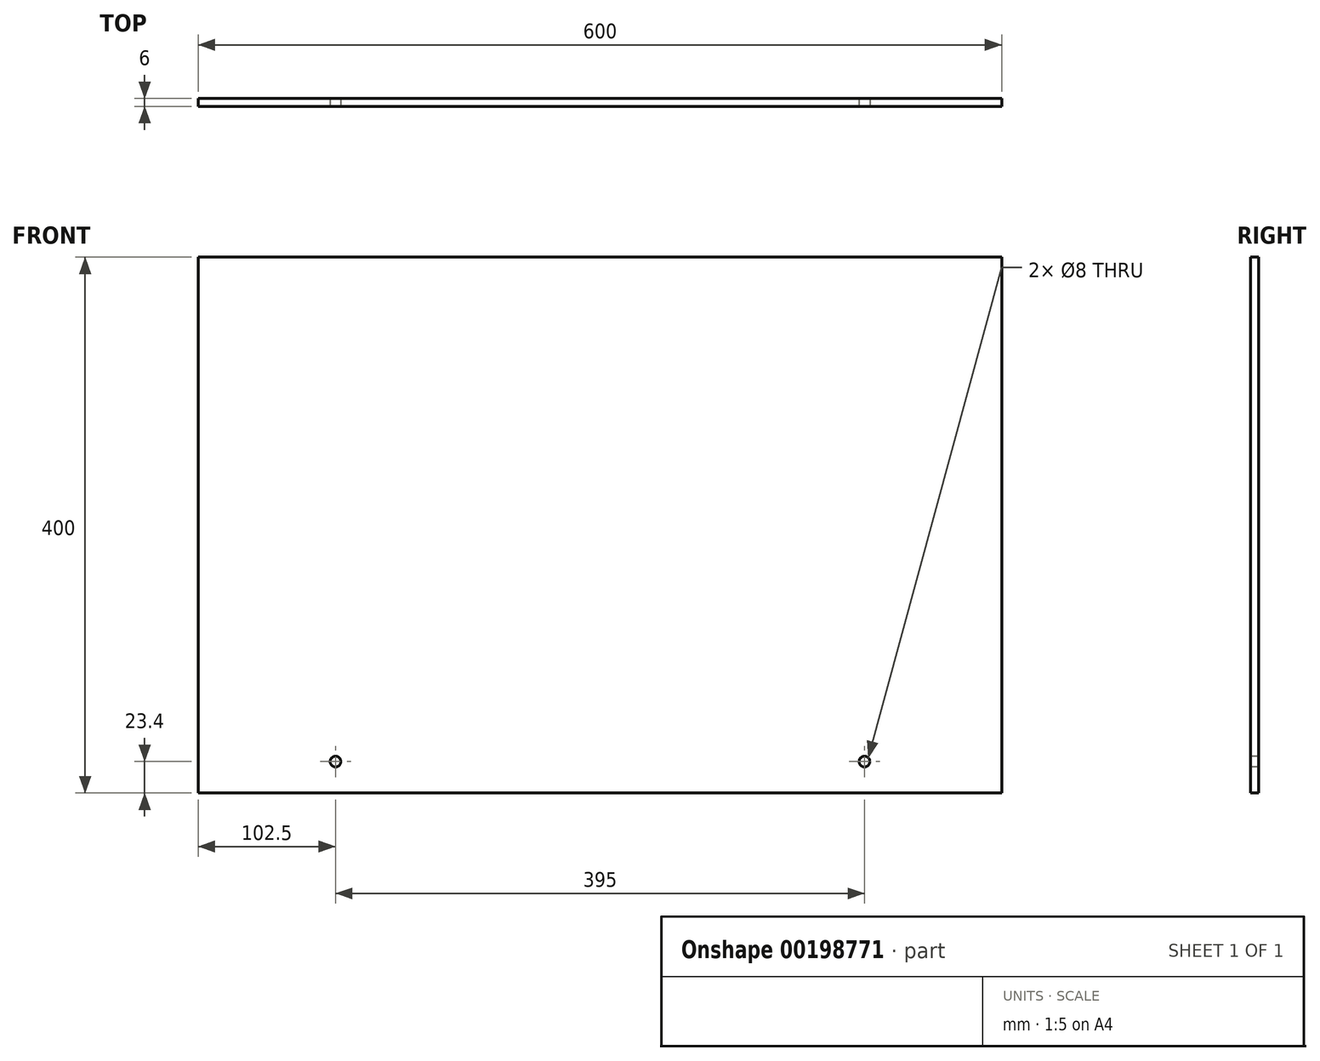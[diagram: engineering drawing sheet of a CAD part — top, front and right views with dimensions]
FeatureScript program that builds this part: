
annotation { "Feature Type Name" : "Feature", "Feature Type Description" : "" }
export const myFeature = defineFeature(function(context is Context, id is Id, definition is map)
    precondition{}
    {
        {
            var Q0;
            Q0=qCreatedBy(makeId("Right.planeOp"),FACE);
            var sketch = newSketch(context, id + "F0", { "sketchPlane" : qUnion([Q0])});
            skLineSegment(sketch, "E0.bottom", {"start": v(3, 200) * mm, "end": v(-3, 200) * mm, "construction": true});
            skLineSegment(sketch, "E0.top", {"start": v(3, -200) * mm, "end": v(-3, -200) * mm});
            skLineSegment(sketch, "E0.left", {"start": v(3, 200) * mm, "end": v(3, -200) * mm});
            skLineSegment(sketch, "E0.right", {"start": v(-3, 200) * mm, "end": v(-3, -200) * mm});
            skPoint(sketch, "E0.middle", {"position": v(0, 0) * mm});
            skLineSegment(sketch, "E1", {"start": v(-3, 200) * mm, "end": v(3, 200) * mm});
            skSolve(sketch);
        }
        {
            var Q0;
            Q0 = qSketchRegion(id + "F0", true);
            extrude(context, id + "F1", {"entities" : qUnion([Q0]), "depth" : 600 * mm, "symmetric" : true});
        }
        {
            var Q0;
            Q0=makeQuery(id+"F1.opExtrude","SWEPT_FACE",FACE,{"disambiguationData":[OSD([sQuery(id+"F0.wireOp",EDGE,"E0.right")])]});
            var sketch = newSketch(context, id + "F2", { "sketchPlane" : qUnion([Q0])});
            skLineSegment(sketch, "E2.0", {"start": v(300, -176.6) * mm, "end": v(-300, -176.6) * mm, "construction": true});
            skLineSegment(sketch, "E3", {"start": v(0, 0) * mm, "end": v(0, -176.6) * mm, "construction": true});
            skCircle(sketch, "E4", {"center": v(-197.5, -176.6) * mm, "radius": 4 * mm});
            skCircle(sketch, "E5.MirrorC", {"center": v(197.5, -176.6) * mm, "radius": 4 * mm});
            skSolve(sketch);
        }
        {
            var Q0;
            Q0 = qSketchRegion(id + "F2", true);
            extrude(context, id + "F3", {"entities" : qUnion([Q0]), "operationType" : NewBodyOperationType.REMOVE, "endBound" : BoundingType.THROUGH_ALL, "oppositeDirection" : true, "depth" : 25 * mm});
        }
    });
